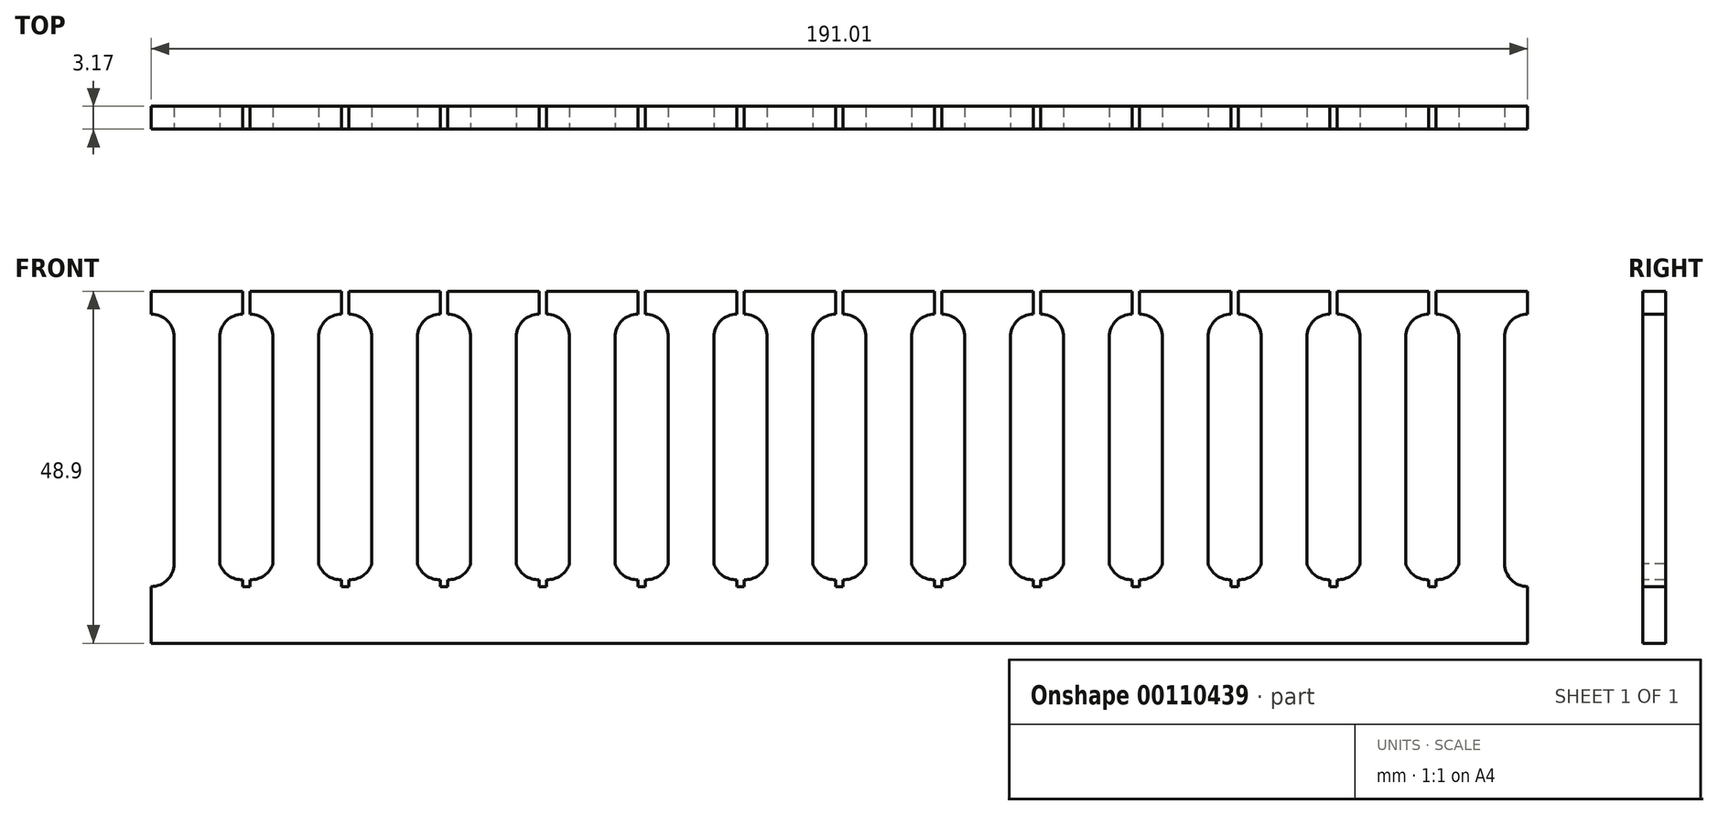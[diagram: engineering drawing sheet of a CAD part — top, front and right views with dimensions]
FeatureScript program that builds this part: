
annotation { "Feature Type Name" : "Feature", "Feature Type Description" : "" }
export const myFeature = defineFeature(function(context is Context, id is Id, definition is map)
    precondition{}
    {
        {
            var Q0;
            Q0=qCreatedBy(makeId("Front.planeOp"),FACE);
            var sketch = newSketch(context, id + "F0", { "sketchPlane" : qUnion([Q0])});
            skLineSegment(sketch, "E0", {"start": v(0, 0) * mm, "end": v(191, 0) * mm});
            skLineSegment(sketch, "E1", {"start": v(191, 0) * mm, "end": v(191, 7.87) * mm});
            skLineSegment(sketch, "E2", {"start": v(0, 7.87) * mm, "end": v(0, 0) * mm});
            skArc(sketch, "E3", {"start": v(187.83, 11.05) * mm, "mid": v(188.76, 8.8) * mm, "end": v(191, 7.87) * mm});
            skLineSegment(sketch, "E4", {"start": v(187.83, 11.05) * mm, "end": v(187.83, 42.55) * mm});
            skArc(sketch, "E5", {"start": v(191, 45.72) * mm, "mid": v(188.76, 44.8) * mm, "end": v(187.83, 42.55) * mm});
            skLineSegment(sketch, "E6", {"start": v(191, 45.72) * mm, "end": v(191, 48.9) * mm});
            skLineSegment(sketch, "E7", {"start": v(191, 48.9) * mm, "end": v(178.3, 48.9) * mm});
            skLineSegment(sketch, "E8", {"start": v(178.3, 48.9) * mm, "end": v(178.3, 45.72) * mm});
            skArc(sketch, "E9", {"start": v(181.48, 42.55) * mm, "mid": v(180.55, 44.8) * mm, "end": v(178.3, 45.72) * mm});
            skLineSegment(sketch, "E10", {"start": v(181.48, 42.55) * mm, "end": v(181.48, 11.05) * mm});
            skArc(sketch, "E11", {"start": v(178.3, 8.82) * mm, "mid": v(180.27, 9.4) * mm, "end": v(181.48, 11.05) * mm});
            skLineSegment(sketch, "E12", {"start": v(178.3, 45.72) * mm, "end": v(178.3, 7.87) * mm, "construction": true});
            skLineSegment(sketch, "E13", {"start": v(177.8, 7.87) * mm, "end": v(177.8, 55.4) * mm, "construction": true});
            skLineSegment(sketch, "E14.MirrorCS", {"start": v(164.6, 45.72) * mm, "end": v(164.6, 48.9) * mm});
            skLineSegment(sketch, "E15.MirrorCS", {"start": v(177.3, 48.9) * mm, "end": v(177.3, 45.72) * mm});
            skArc(sketch, "E16.MirrorCS", {"start": v(177.3, 8.82) * mm, "mid": v(175.33, 9.4) * mm, "end": v(174.12, 11.05) * mm});
            skArc(sketch, "E17.MirrorCS", {"start": v(167.77, 11.05) * mm, "mid": v(166.56, 9.4) * mm, "end": v(164.6, 8.82) * mm});
            skArc(sketch, "E18.MirrorCS", {"start": v(164.6, 45.72) * mm, "mid": v(166.84, 44.8) * mm, "end": v(167.77, 42.55) * mm});
            skLineSegment(sketch, "E19.MirrorCS", {"start": v(177.3, 45.72) * mm, "end": v(177.3, 7.87) * mm, "construction": true});
            skLineSegment(sketch, "E20.MirrorCS", {"start": v(164.6, 48.9) * mm, "end": v(177.3, 48.9) * mm});
            skArc(sketch, "E21.MirrorCS", {"start": v(174.12, 42.55) * mm, "mid": v(175.05, 44.8) * mm, "end": v(177.3, 45.72) * mm});
            skLineSegment(sketch, "E22.MirrorCS", {"start": v(174.12, 42.55) * mm, "end": v(174.12, 11.05) * mm});
            skLineSegment(sketch, "E23.MirrorCS", {"start": v(167.77, 11.05) * mm, "end": v(167.77, 42.55) * mm});
            skLineSegment(sketch, "E24", {"start": v(177.3, 8.82) * mm, "end": v(177.3, 7.87) * mm});
            skLineSegment(sketch, "E25", {"start": v(178.3, 7.87) * mm, "end": v(178.3, 8.82) * mm});
            skLineSegment(sketch, "E26", {"start": v(177.3, 7.87) * mm, "end": v(178.3, 7.87) * mm});
            skLineSegment(sketch, "E27", {"start": v(164.6, 45.72) * mm, "end": v(164.6, 7.87) * mm, "construction": true});
            skLineSegment(sketch, "E28", {"start": v(164.6, 8.82) * mm, "end": v(164.6, 7.87) * mm});
            skLineSegment(sketch, "E29", {"start": v(164.08, 51.17) * mm, "end": v(164.08, 7.87) * mm, "construction": true});
            skLineSegment(sketch, "E30.MirrorCS", {"start": v(150.88, 48.9) * mm, "end": v(150.88, 45.72) * mm});
            skArc(sketch, "E31.MirrorCS", {"start": v(160.4, 11.05) * mm, "mid": v(161.6, 9.4) * mm, "end": v(163.58, 8.82) * mm});
            skLineSegment(sketch, "E32.MirrorCS", {"start": v(154.05, 42.55) * mm, "end": v(154.05, 11.05) * mm});
            skArc(sketch, "E33.MirrorCS", {"start": v(154.05, 42.55) * mm, "mid": v(153.12, 44.8) * mm, "end": v(150.88, 45.72) * mm});
            skLineSegment(sketch, "E34.MirrorCS", {"start": v(150.88, 45.72) * mm, "end": v(150.88, 7.87) * mm, "construction": true});
            skLineSegment(sketch, "E35.MirrorCS", {"start": v(163.58, 45.72) * mm, "end": v(163.58, 48.9) * mm});
            skArc(sketch, "E36.MirrorCS", {"start": v(163.58, 45.72) * mm, "mid": v(161.33, 44.8) * mm, "end": v(160.4, 42.55) * mm});
            skArc(sketch, "E37.MirrorCS", {"start": v(150.88, 8.82) * mm, "mid": v(152.84, 9.4) * mm, "end": v(154.05, 11.05) * mm});
            skLineSegment(sketch, "E38.MirrorCS", {"start": v(160.4, 11.05) * mm, "end": v(160.4, 42.55) * mm});
            skLineSegment(sketch, "E39.MirrorCS", {"start": v(163.58, 45.72) * mm, "end": v(163.58, 7.87) * mm, "construction": true});
            skLineSegment(sketch, "E40.MirrorCS", {"start": v(163.58, 48.9) * mm, "end": v(150.88, 48.9) * mm});
            skLineSegment(sketch, "E41", {"start": v(150.37, 50.6) * mm, "end": v(150.37, 7.87) * mm, "construction": true});
            skLineSegment(sketch, "E42.MirrorCS", {"start": v(123.44, 8.82) * mm, "end": v(123.44, 7.87) * mm});
            skLineSegment(sketch, "E43.MirrorCS", {"start": v(136.14, 8.82) * mm, "end": v(136.14, 7.87) * mm});
            skLineSegment(sketch, "E44.MirrorCS", {"start": v(137.16, 45.72) * mm, "end": v(137.16, 48.9) * mm});
            skLineSegment(sketch, "E45.MirrorCS", {"start": v(136.14, 45.72) * mm, "end": v(136.14, 48.9) * mm});
            skArc(sketch, "E46.MirrorCS", {"start": v(140.34, 11.05) * mm, "mid": v(139.13, 9.4) * mm, "end": v(137.16, 8.82) * mm});
            skLineSegment(sketch, "E47.MirrorCS", {"start": v(123.44, 48.9) * mm, "end": v(123.44, 45.72) * mm});
            skArc(sketch, "E48.MirrorCS", {"start": v(146.68, 42.55) * mm, "mid": v(147.61, 44.8) * mm, "end": v(149.86, 45.72) * mm});
            skArc(sketch, "E49.MirrorCS", {"start": v(132.97, 11.05) * mm, "mid": v(134.18, 9.4) * mm, "end": v(136.14, 8.82) * mm});
            skLineSegment(sketch, "E50.MirrorCS", {"start": v(123.44, 45.72) * mm, "end": v(123.44, 7.87) * mm, "construction": true});
            skArc(sketch, "E51.MirrorCS", {"start": v(149.86, 8.82) * mm, "mid": v(147.9, 9.4) * mm, "end": v(146.68, 11.05) * mm});
            skLineSegment(sketch, "E52.MirrorCS", {"start": v(149.86, 48.9) * mm, "end": v(149.86, 45.72) * mm});
            skArc(sketch, "E53.MirrorCS", {"start": v(126.62, 42.55) * mm, "mid": v(125.69, 44.8) * mm, "end": v(123.44, 45.72) * mm});
            skLineSegment(sketch, "E54.MirrorCS", {"start": v(137.16, 48.9) * mm, "end": v(149.86, 48.9) * mm});
            skLineSegment(sketch, "E55.MirrorCS", {"start": v(126.62, 42.55) * mm, "end": v(126.62, 11.05) * mm});
            skLineSegment(sketch, "E56.MirrorCS", {"start": v(140.34, 11.05) * mm, "end": v(140.34, 42.55) * mm});
            skLineSegment(sketch, "E57.MirrorCS", {"start": v(137.16, 45.72) * mm, "end": v(137.16, 7.87) * mm, "construction": true});
            skLineSegment(sketch, "E58.MirrorCS", {"start": v(132.97, 11.05) * mm, "end": v(132.97, 42.55) * mm});
            skLineSegment(sketch, "E59.MirrorCS", {"start": v(146.68, 42.55) * mm, "end": v(146.68, 11.05) * mm});
            skLineSegment(sketch, "E60.MirrorCS", {"start": v(136.14, 45.72) * mm, "end": v(136.14, 7.87) * mm, "construction": true});
            skArc(sketch, "E61.MirrorCS", {"start": v(136.14, 45.72) * mm, "mid": v(133.9, 44.8) * mm, "end": v(132.97, 42.55) * mm});
            skLineSegment(sketch, "E62.MirrorCS", {"start": v(136.14, 48.9) * mm, "end": v(123.44, 48.9) * mm});
            skArc(sketch, "E63.MirrorCS", {"start": v(123.44, 8.82) * mm, "mid": v(125.41, 9.4) * mm, "end": v(126.62, 11.05) * mm});
            skLineSegment(sketch, "E64.MirrorCS", {"start": v(136.65, 51.17) * mm, "end": v(136.65, 7.87) * mm, "construction": true});
            skLineSegment(sketch, "E65.MirrorCS", {"start": v(149.86, 45.72) * mm, "end": v(149.86, 7.87) * mm, "construction": true});
            skArc(sketch, "E66.MirrorCS", {"start": v(137.16, 45.72) * mm, "mid": v(139.4, 44.8) * mm, "end": v(140.33, 42.55) * mm});
            skLineSegment(sketch, "E67", {"start": v(122.94, 50.8) * mm, "end": v(122.94, 7.87) * mm, "construction": true});
            skLineSegment(sketch, "E68.MirrorCS", {"start": v(68.58, 7.87) * mm, "end": v(67.56, 7.87) * mm});
            skLineSegment(sketch, "E69.MirrorCS", {"start": v(122.43, 8.82) * mm, "end": v(122.43, 7.87) * mm});
            skLineSegment(sketch, "E70.MirrorCS", {"start": v(109.73, 8.82) * mm, "end": v(109.73, 7.87) * mm});
            skLineSegment(sketch, "E71.MirrorCS", {"start": v(122.43, 48.9) * mm, "end": v(122.43, 45.72) * mm});
            skLineSegment(sketch, "E72.MirrorCS", {"start": v(108.71, 45.72) * mm, "end": v(108.71, 48.9) * mm});
            skLineSegment(sketch, "E73.MirrorCS", {"start": v(109.73, 45.72) * mm, "end": v(109.73, 48.9) * mm});
            skLineSegment(sketch, "E74.MirrorCS", {"start": v(96.01, 48.9) * mm, "end": v(96.01, 45.72) * mm});
            skLineSegment(sketch, "E75.MirrorCS", {"start": v(95.5, 50.6) * mm, "end": v(95.5, 7.87) * mm, "construction": true});
            skLineSegment(sketch, "E76.MirrorCS", {"start": v(109.73, 48.9) * mm, "end": v(122.43, 48.9) * mm});
            skLineSegment(sketch, "E77.MirrorCS", {"start": v(108.71, 45.72) * mm, "end": v(108.71, 7.87) * mm, "construction": true});
            skLineSegment(sketch, "E78.MirrorCS", {"start": v(96.01, 45.72) * mm, "end": v(96.01, 7.87) * mm, "construction": true});
            skLineSegment(sketch, "E79.MirrorCS", {"start": v(122.43, 45.72) * mm, "end": v(122.43, 7.87) * mm, "construction": true});
            skLineSegment(sketch, "E80.MirrorCS", {"start": v(119.25, 42.55) * mm, "end": v(119.25, 11.05) * mm});
            skArc(sketch, "E81.MirrorCS", {"start": v(122.43, 8.82) * mm, "mid": v(120.46, 9.4) * mm, "end": v(119.25, 11.05) * mm});
            skArc(sketch, "E82.MirrorCS", {"start": v(99.19, 42.55) * mm, "mid": v(98.26, 44.8) * mm, "end": v(96.01, 45.72) * mm});
            skLineSegment(sketch, "E83.MirrorCS", {"start": v(105.54, 11.05) * mm, "end": v(105.54, 42.55) * mm});
            skLineSegment(sketch, "E84.MirrorCS", {"start": v(109.22, 51.17) * mm, "end": v(109.22, 7.87) * mm, "construction": true});
            skArc(sketch, "E85.MirrorCS", {"start": v(112.9, 11.05) * mm, "mid": v(111.7, 9.4) * mm, "end": v(109.73, 8.82) * mm});
            skLineSegment(sketch, "E86.MirrorCS", {"start": v(112.9, 11.05) * mm, "end": v(112.9, 42.55) * mm});
            skArc(sketch, "E87.MirrorCS", {"start": v(108.71, 45.72) * mm, "mid": v(106.47, 44.8) * mm, "end": v(105.54, 42.55) * mm});
            skLineSegment(sketch, "E88.MirrorCS", {"start": v(109.73, 45.72) * mm, "end": v(109.73, 7.87) * mm, "construction": true});
            skArc(sketch, "E89.MirrorCS", {"start": v(96.01, 8.82) * mm, "mid": v(97.98, 9.4) * mm, "end": v(99.19, 11.05) * mm});
            skLineSegment(sketch, "E90.MirrorCS", {"start": v(99.19, 42.55) * mm, "end": v(99.19, 11.05) * mm});
            skLineSegment(sketch, "E91.MirrorCS", {"start": v(108.71, 48.9) * mm, "end": v(96.01, 48.9) * mm});
            skArc(sketch, "E92.MirrorCS", {"start": v(105.54, 11.05) * mm, "mid": v(106.75, 9.4) * mm, "end": v(108.71, 8.82) * mm});
            skArc(sketch, "E93.MirrorCS", {"start": v(119.25, 42.55) * mm, "mid": v(120.18, 44.8) * mm, "end": v(122.43, 45.72) * mm});
            skArc(sketch, "E94.MirrorCS", {"start": v(109.73, 45.72) * mm, "mid": v(111.97, 44.8) * mm, "end": v(112.9, 42.55) * mm});
            skLineSegment(sketch, "E95.MirrorCS", {"start": v(13.72, 8.82) * mm, "end": v(13.72, 7.87) * mm});
            skLineSegment(sketch, "E96.MirrorCS", {"start": v(13.72, 7.87) * mm, "end": v(12.7, 7.87) * mm});
            skLineSegment(sketch, "E97.MirrorCS", {"start": v(12.7, 7.87) * mm, "end": v(12.7, 8.82) * mm});
            skLineSegment(sketch, "E98.MirrorCS", {"start": v(67.56, 8.82) * mm, "end": v(67.56, 7.87) * mm});
            skLineSegment(sketch, "E99.MirrorCS", {"start": v(81.28, 8.82) * mm, "end": v(81.28, 7.87) * mm});
            skLineSegment(sketch, "E100.MirrorCS", {"start": v(68.58, 8.82) * mm, "end": v(68.58, 7.87) * mm});
            skLineSegment(sketch, "E101.MirrorCS", {"start": v(54.86, 8.82) * mm, "end": v(54.86, 7.87) * mm});
            skLineSegment(sketch, "E102.MirrorCS", {"start": v(0, 0) * mm, "end": v(0, 7.87) * mm});
            skLineSegment(sketch, "E103.MirrorCS", {"start": v(13.72, 48.9) * mm, "end": v(13.72, 45.72) * mm});
            skLineSegment(sketch, "E104.MirrorCS", {"start": v(67.56, 48.9) * mm, "end": v(67.56, 45.72) * mm});
            skLineSegment(sketch, "E105.MirrorCS", {"start": v(27.43, 45.72) * mm, "end": v(27.43, 48.9) * mm});
            skLineSegment(sketch, "E106.MirrorCS", {"start": v(53.85, 45.72) * mm, "end": v(53.85, 48.9) * mm});
            skLineSegment(sketch, "E107.MirrorCS", {"start": v(26.42, 8.82) * mm, "end": v(26.42, 7.87) * mm});
            skArc(sketch, "E108.MirrorCS", {"start": v(41.15, 8.82) * mm, "mid": v(43.11, 9.4) * mm, "end": v(44.32, 11.05) * mm});
            skLineSegment(sketch, "E109.MirrorCS", {"start": v(81.28, 45.72) * mm, "end": v(81.28, 48.9) * mm});
            skLineSegment(sketch, "E110.MirrorCS", {"start": v(95, 48.9) * mm, "end": v(95, 45.72) * mm});
            skLineSegment(sketch, "E111.MirrorCS", {"start": v(54.86, 45.72) * mm, "end": v(54.86, 48.9) * mm});
            skLineSegment(sketch, "E112.MirrorCS", {"start": v(41.15, 48.9) * mm, "end": v(41.15, 45.72) * mm});
            skLineSegment(sketch, "E113.MirrorCS", {"start": v(82.3, 45.72) * mm, "end": v(82.3, 48.9) * mm});
            skLineSegment(sketch, "E114.MirrorCS", {"start": v(0, 45.72) * mm, "end": v(0, 48.9) * mm});
            skLineSegment(sketch, "E115.MirrorCS", {"start": v(26.42, 45.72) * mm, "end": v(26.42, 48.9) * mm});
            skLineSegment(sketch, "E116.MirrorCS", {"start": v(68.58, 48.9) * mm, "end": v(68.58, 45.72) * mm});
            skLineSegment(sketch, "E117.MirrorCS", {"start": v(40.13, 48.9) * mm, "end": v(40.13, 45.72) * mm});
            skLineSegment(sketch, "E118.MirrorCS", {"start": v(12.7, 48.9) * mm, "end": v(12.7, 45.72) * mm});
            skArc(sketch, "E119.MirrorCS", {"start": v(27.43, 45.72) * mm, "mid": v(29.68, 44.8) * mm, "end": v(30.6, 42.55) * mm});
            skLineSegment(sketch, "E120.MirrorCS", {"start": v(40.64, 50.6) * mm, "end": v(40.64, 7.87) * mm, "construction": true});
            skLineSegment(sketch, "E121.MirrorCS", {"start": v(53.85, 45.72) * mm, "end": v(53.85, 7.87) * mm, "construction": true});
            skLineSegment(sketch, "E122.MirrorCS", {"start": v(12.7, 45.72) * mm, "end": v(12.7, 7.87) * mm, "construction": true});
            skLineSegment(sketch, "E123.MirrorCS", {"start": v(54.86, 48.9) * mm, "end": v(67.56, 48.9) * mm});
            skLineSegment(sketch, "E124.MirrorCS", {"start": v(82.3, 45.72) * mm, "end": v(82.3, 7.87) * mm, "construction": true});
            skArc(sketch, "E125.MirrorCS", {"start": v(13.72, 8.82) * mm, "mid": v(15.68, 9.4) * mm, "end": v(16.9, 11.05) * mm});
            skArc(sketch, "E126.MirrorCS", {"start": v(30.6, 11.05) * mm, "mid": v(29.4, 9.4) * mm, "end": v(27.43, 8.82) * mm});
            skLineSegment(sketch, "E127.MirrorCS", {"start": v(91.82, 42.55) * mm, "end": v(91.82, 11.05) * mm});
            skLineSegment(sketch, "E128.MirrorCS", {"start": v(44.32, 42.55) * mm, "end": v(44.32, 11.05) * mm});
            skLineSegment(sketch, "E129.MirrorCS", {"start": v(95, 45.72) * mm, "end": v(95, 7.87) * mm, "construction": true});
            skLineSegment(sketch, "E130.MirrorCS", {"start": v(54.86, 45.72) * mm, "end": v(54.86, 7.87) * mm, "construction": true});
            skArc(sketch, "E131.MirrorCS", {"start": v(68.58, 8.82) * mm, "mid": v(70.55, 9.4) * mm, "end": v(71.76, 11.05) * mm});
            skArc(sketch, "E132.MirrorCS", {"start": v(53.85, 45.72) * mm, "mid": v(51.6, 44.8) * mm, "end": v(50.67, 42.55) * mm});
            skLineSegment(sketch, "E133.MirrorCS", {"start": v(26.42, 45.72) * mm, "end": v(26.42, 7.87) * mm, "construction": true});
            skArc(sketch, "E134.MirrorCS", {"start": v(95, 8.82) * mm, "mid": v(93.03, 9.4) * mm, "end": v(91.82, 11.05) * mm});
            skLineSegment(sketch, "E135.MirrorCS", {"start": v(13.72, 45.72) * mm, "end": v(13.72, 7.87) * mm, "construction": true});
            skLineSegment(sketch, "E136.MirrorCS", {"start": v(26.42, 48.9) * mm, "end": v(13.72, 48.9) * mm});
            skArc(sketch, "E137.MirrorCS", {"start": v(91.82, 42.55) * mm, "mid": v(92.75, 44.8) * mm, "end": v(95, 45.72) * mm});
            skLineSegment(sketch, "E138.MirrorCS", {"start": v(68.07, 50.8) * mm, "end": v(68.07, 7.87) * mm, "construction": true});
            skArc(sketch, "E139.MirrorCS", {"start": v(54.86, 45.72) * mm, "mid": v(57.1, 44.8) * mm, "end": v(58.04, 42.55) * mm});
            skLineSegment(sketch, "E140.MirrorCS", {"start": v(26.92, 51.17) * mm, "end": v(26.92, 7.87) * mm, "construction": true});
            skLineSegment(sketch, "E141.MirrorCS", {"start": v(81.28, 45.72) * mm, "end": v(81.28, 7.87) * mm, "construction": true});
            skArc(sketch, "E142.MirrorCS", {"start": v(67.56, 8.82) * mm, "mid": v(65.6, 9.4) * mm, "end": v(64.39, 11.05) * mm});
            skLineSegment(sketch, "E143.MirrorCS", {"start": v(58.04, 11.05) * mm, "end": v(58.04, 42.55) * mm});
            skLineSegment(sketch, "E144.MirrorCS", {"start": v(71.76, 42.55) * mm, "end": v(71.76, 11.05) * mm});
            skArc(sketch, "E145.MirrorCS", {"start": v(36.96, 42.55) * mm, "mid": v(37.89, 44.8) * mm, "end": v(40.13, 45.72) * mm});
            skLineSegment(sketch, "E146.MirrorCS", {"start": v(3.18, 11.05) * mm, "end": v(3.18, 42.55) * mm});
            skArc(sketch, "E147.MirrorCS", {"start": v(3.18, 11.05) * mm, "mid": v(2.25, 8.8) * mm, "end": v(0, 7.87) * mm});
            skArc(sketch, "E148.MirrorCS", {"start": v(44.32, 42.55) * mm, "mid": v(43.4, 44.8) * mm, "end": v(41.15, 45.72) * mm});
            skArc(sketch, "E149.MirrorCS", {"start": v(26.42, 45.72) * mm, "mid": v(24.17, 44.8) * mm, "end": v(23.24, 42.55) * mm});
            skArc(sketch, "E150.MirrorCS", {"start": v(0, 45.72) * mm, "mid": v(2.25, 44.8) * mm, "end": v(3.18, 42.55) * mm});
            skArc(sketch, "E151.MirrorCS", {"start": v(82.3, 45.72) * mm, "mid": v(84.54, 44.8) * mm, "end": v(85.47, 42.55) * mm});
            skArc(sketch, "E152.MirrorCS", {"start": v(81.28, 45.72) * mm, "mid": v(79.03, 44.8) * mm, "end": v(78.1, 42.55) * mm});
            skLineSegment(sketch, "E153.MirrorCS", {"start": v(81.79, 51.17) * mm, "end": v(81.79, 7.87) * mm, "construction": true});
            skLineSegment(sketch, "E154.MirrorCS", {"start": v(36.96, 42.55) * mm, "end": v(36.96, 11.05) * mm});
            skLineSegment(sketch, "E155.MirrorCS", {"start": v(16.9, 42.55) * mm, "end": v(16.9, 11.05) * mm});
            skLineSegment(sketch, "E156.MirrorCS", {"start": v(13.2, 7.87) * mm, "end": v(13.2, 55.4) * mm, "construction": true});
            skLineSegment(sketch, "E157.MirrorCS", {"start": v(82.3, 48.9) * mm, "end": v(95, 48.9) * mm});
            skArc(sketch, "E158.MirrorCS", {"start": v(85.47, 11.05) * mm, "mid": v(84.26, 9.4) * mm, "end": v(82.3, 8.82) * mm});
            skArc(sketch, "E159.MirrorCS", {"start": v(78.1, 11.05) * mm, "mid": v(79.31, 9.4) * mm, "end": v(81.28, 8.82) * mm});
            skLineSegment(sketch, "E160.MirrorCS", {"start": v(64.39, 42.55) * mm, "end": v(64.39, 11.05) * mm});
            skLineSegment(sketch, "E161.MirrorCS", {"start": v(78.1, 11.05) * mm, "end": v(78.1, 42.55) * mm});
            skArc(sketch, "E162.MirrorCS", {"start": v(64.39, 42.55) * mm, "mid": v(65.32, 44.8) * mm, "end": v(67.56, 45.72) * mm});
            skArc(sketch, "E163.MirrorCS", {"start": v(40.13, 8.82) * mm, "mid": v(38.17, 9.4) * mm, "end": v(36.96, 11.05) * mm});
            skArc(sketch, "E164.MirrorCS", {"start": v(50.67, 11.05) * mm, "mid": v(51.88, 9.4) * mm, "end": v(53.85, 8.82) * mm});
            skLineSegment(sketch, "E165.MirrorCS", {"start": v(9.52, 42.55) * mm, "end": v(9.52, 11.05) * mm});
            skLineSegment(sketch, "E166.MirrorCS", {"start": v(68.58, 45.72) * mm, "end": v(68.58, 7.87) * mm, "construction": true});
            skLineSegment(sketch, "E167.MirrorCS", {"start": v(53.85, 48.9) * mm, "end": v(41.15, 48.9) * mm});
            skLineSegment(sketch, "E168.MirrorCS", {"start": v(54.36, 51.17) * mm, "end": v(54.36, 7.87) * mm, "construction": true});
            skLineSegment(sketch, "E169.MirrorCS", {"start": v(40.13, 45.72) * mm, "end": v(40.13, 7.87) * mm, "construction": true});
            skLineSegment(sketch, "E170.MirrorCS", {"start": v(27.43, 45.72) * mm, "end": v(27.43, 7.87) * mm, "construction": true});
            skLineSegment(sketch, "E171.MirrorCS", {"start": v(27.43, 48.9) * mm, "end": v(40.13, 48.9) * mm});
            skLineSegment(sketch, "E172.MirrorCS", {"start": v(50.67, 11.05) * mm, "end": v(50.67, 42.55) * mm});
            skArc(sketch, "E173.MirrorCS", {"start": v(9.52, 42.55) * mm, "mid": v(10.45, 44.8) * mm, "end": v(12.7, 45.72) * mm});
            skArc(sketch, "E174.MirrorCS", {"start": v(16.9, 42.55) * mm, "mid": v(15.96, 44.8) * mm, "end": v(13.72, 45.72) * mm});
            skLineSegment(sketch, "E175.MirrorCS", {"start": v(0, 48.9) * mm, "end": v(12.7, 48.9) * mm});
            skLineSegment(sketch, "E176.MirrorCS", {"start": v(81.28, 48.9) * mm, "end": v(68.58, 48.9) * mm});
            skArc(sketch, "E177.MirrorCS", {"start": v(58.04, 11.05) * mm, "mid": v(56.83, 9.4) * mm, "end": v(54.86, 8.82) * mm});
            skLineSegment(sketch, "E178.MirrorCS", {"start": v(30.6, 11.05) * mm, "end": v(30.6, 42.55) * mm});
            skArc(sketch, "E179.MirrorCS", {"start": v(71.76, 42.55) * mm, "mid": v(70.83, 44.8) * mm, "end": v(68.58, 45.72) * mm});
            skLineSegment(sketch, "E180.MirrorCS", {"start": v(41.15, 45.72) * mm, "end": v(41.15, 7.87) * mm, "construction": true});
            skLineSegment(sketch, "E181.MirrorCS", {"start": v(23.24, 11.05) * mm, "end": v(23.24, 42.55) * mm});
            skLineSegment(sketch, "E182.MirrorCS", {"start": v(67.56, 45.72) * mm, "end": v(67.56, 7.87) * mm, "construction": true});
            skArc(sketch, "E183.MirrorCS", {"start": v(23.24, 11.05) * mm, "mid": v(24.45, 9.4) * mm, "end": v(26.42, 8.82) * mm});
            skLineSegment(sketch, "E184.MirrorCS", {"start": v(85.47, 11.05) * mm, "end": v(85.47, 42.55) * mm});
            skArc(sketch, "E185.MirrorCS", {"start": v(12.7, 8.82) * mm, "mid": v(10.73, 9.4) * mm, "end": v(9.52, 11.05) * mm});
            skLineSegment(sketch, "E186", {"start": v(26.42, 7.87) * mm, "end": v(27.43, 7.87) * mm});
            skLineSegment(sketch, "E187", {"start": v(40.13, 7.87) * mm, "end": v(41.15, 7.87) * mm});
            skLineSegment(sketch, "E188", {"start": v(53.85, 7.87) * mm, "end": v(54.86, 7.87) * mm});
            skLineSegment(sketch, "E189", {"start": v(81.28, 7.87) * mm, "end": v(82.3, 7.87) * mm});
            skLineSegment(sketch, "E190", {"start": v(95, 7.87) * mm, "end": v(96.01, 7.87) * mm});
            skLineSegment(sketch, "E191", {"start": v(122.43, 7.87) * mm, "end": v(123.44, 7.87) * mm});
            skLineSegment(sketch, "E192", {"start": v(136.14, 7.87) * mm, "end": v(137.16, 7.87) * mm});
            skLineSegment(sketch, "E193", {"start": v(163.58, 7.87) * mm, "end": v(164.6, 7.87) * mm});
            skLineSegment(sketch, "E194", {"start": v(149.86, 7.87) * mm, "end": v(150.88, 7.87) * mm});
            skLineSegment(sketch, "E195", {"start": v(108.71, 7.87) * mm, "end": v(109.73, 7.87) * mm});
            skLineSegment(sketch, "E196", {"start": v(108.71, 7.87) * mm, "end": v(108.71, 8.82) * mm});
            skLineSegment(sketch, "E197", {"start": v(137.16, 7.87) * mm, "end": v(137.16, 8.82) * mm});
            skLineSegment(sketch, "E198", {"start": v(149.86, 7.87) * mm, "end": v(149.86, 8.82) * mm});
            skLineSegment(sketch, "E199", {"start": v(150.88, 7.87) * mm, "end": v(150.88, 8.82) * mm});
            skLineSegment(sketch, "E200", {"start": v(163.58, 7.87) * mm, "end": v(163.58, 8.82) * mm});
            skLineSegment(sketch, "E201", {"start": v(96.01, 7.87) * mm, "end": v(96.01, 8.82) * mm});
            skLineSegment(sketch, "E202", {"start": v(95, 7.87) * mm, "end": v(95, 8.82) * mm});
            skLineSegment(sketch, "E203", {"start": v(82.3, 7.87) * mm, "end": v(82.3, 8.82) * mm});
            skLineSegment(sketch, "E204", {"start": v(53.85, 7.87) * mm, "end": v(53.85, 8.82) * mm});
            skLineSegment(sketch, "E205", {"start": v(41.15, 7.87) * mm, "end": v(41.15, 8.82) * mm});
            skLineSegment(sketch, "E206", {"start": v(40.13, 7.87) * mm, "end": v(40.13, 8.82) * mm});
            skLineSegment(sketch, "E207", {"start": v(27.43, 7.87) * mm, "end": v(27.43, 8.82) * mm});
            skSolve(sketch);
        }
        {
            var Q0;
            Q0 = qSketchRegion(id + "F0", true);
            extrude(context, id + "F1", {"entities" : qUnion([Q0]), "oppositeDirection" : true, "depth" : 3.17 * mm});
        }
    });
